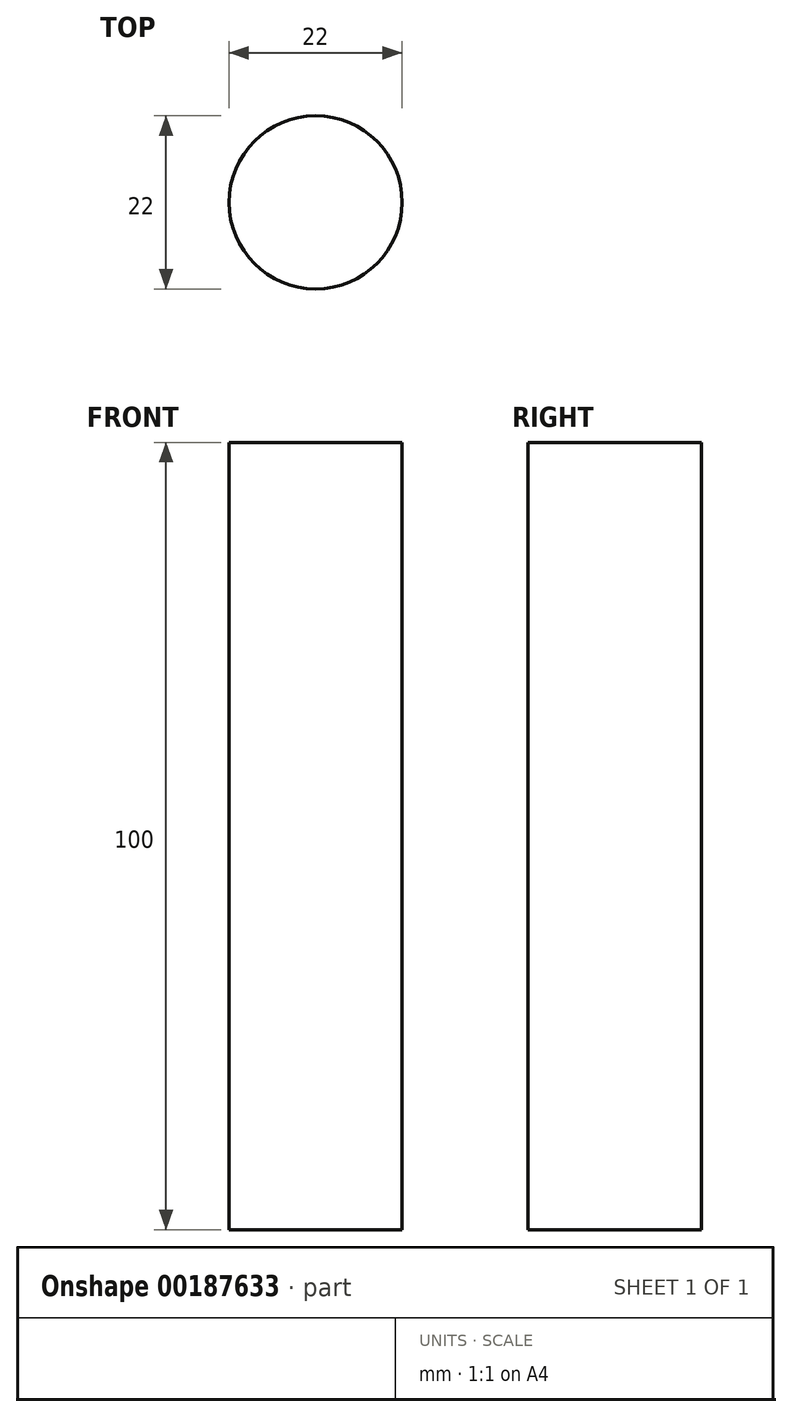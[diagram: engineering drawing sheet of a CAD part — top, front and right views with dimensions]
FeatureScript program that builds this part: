
annotation { "Feature Type Name" : "Feature", "Feature Type Description" : "" }
export const myFeature = defineFeature(function(context is Context, id is Id, definition is map)
    precondition{}
    {
        {
            var Q0;
            Q0=qCreatedBy(makeId("Top.planeOp"),FACE);
            var sketch = newSketch(context, id + "F0", { "sketchPlane" : qUnion([Q0])});
            skCircle(sketch, "E0", {"center": v(0, 0) * mm, "radius": 11 * mm});
            skSolve(sketch);
        }
        {
            var Q0;
            Q0 = qSketchRegion(id + "F0", true);
            extrude(context, id + "F1", {"entities" : qUnion([Q0]), "depth" : 100 * mm});
        }
    });
